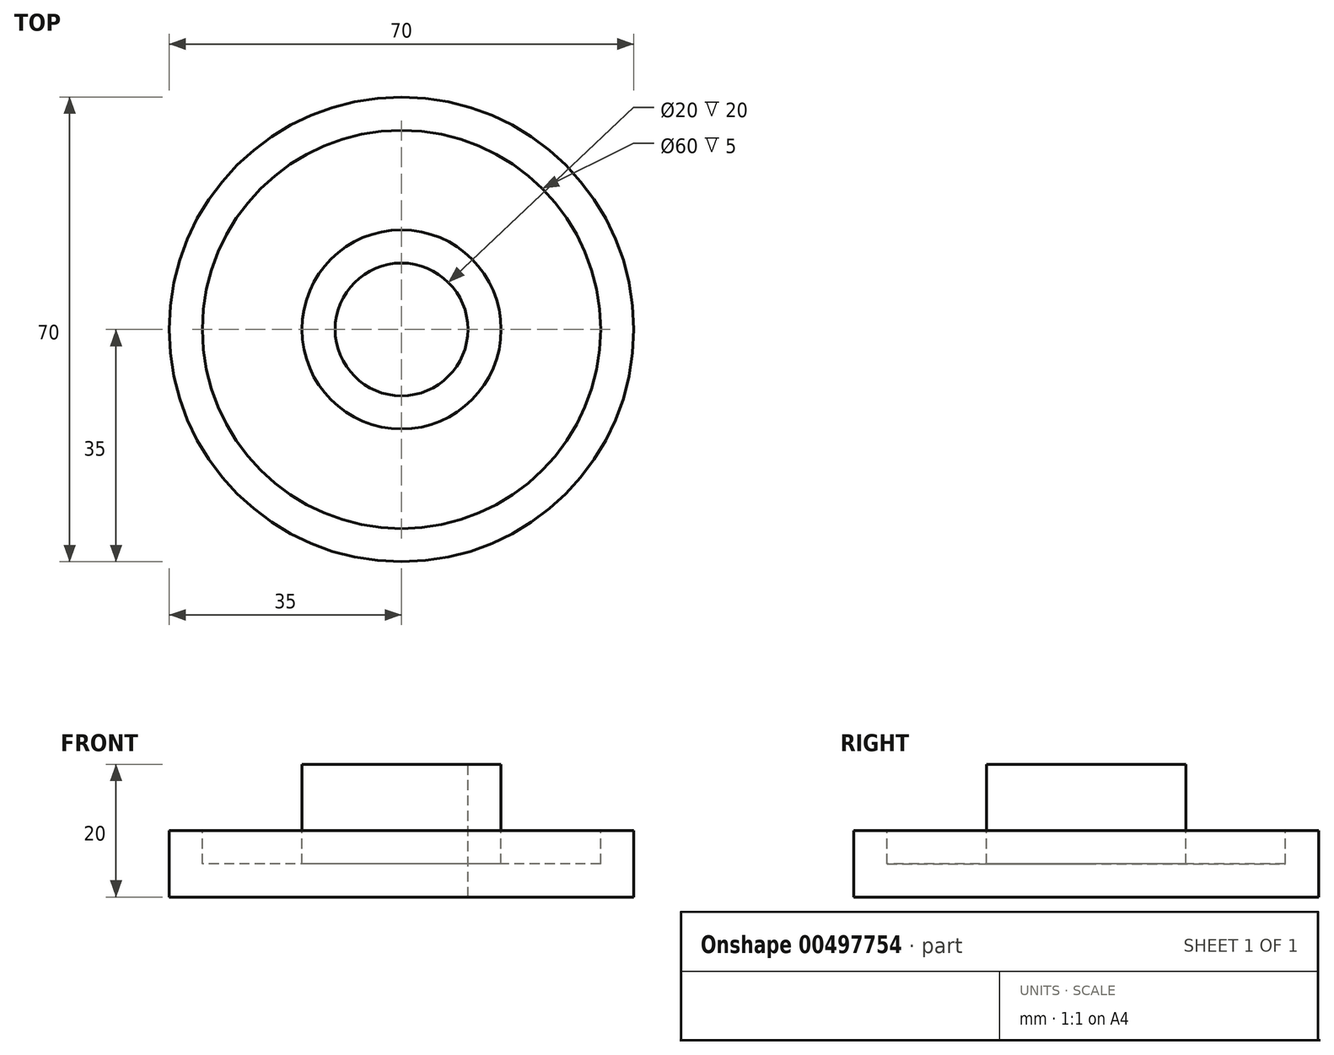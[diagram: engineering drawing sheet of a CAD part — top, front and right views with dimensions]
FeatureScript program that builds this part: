
annotation { "Feature Type Name" : "Feature", "Feature Type Description" : "" }
export const myFeature = defineFeature(function(context is Context, id is Id, definition is map)
    precondition{}
    {
        {
            var Q0;
            Q0=qCreatedBy(makeId("Front.planeOp"),FACE);
            var sketch = newSketch(context, id + "F0", { "sketchPlane" : qUnion([Q0])});
            skLineSegment(sketch, "E0", {"start": v(10, 20) * mm, "end": v(10, 0) * mm});
            skLineSegment(sketch, "E1", {"start": v(10, 0) * mm, "end": v(35, 0) * mm});
            skLineSegment(sketch, "E2", {"start": v(35, 0) * mm, "end": v(35, 10) * mm});
            skLineSegment(sketch, "E3", {"start": v(35, 10) * mm, "end": v(30, 10) * mm});
            skLineSegment(sketch, "E4", {"start": v(30, 10) * mm, "end": v(30, 5) * mm});
            skLineSegment(sketch, "E5", {"start": v(30, 5) * mm, "end": v(15, 5) * mm});
            skLineSegment(sketch, "E6", {"start": v(15, 5) * mm, "end": v(15, 20) * mm});
            skLineSegment(sketch, "E7", {"start": v(15, 20) * mm, "end": v(10, 20) * mm});
            skLineSegment(sketch, "E8", {"start": v(0, 60.65) * mm, "end": v(0, -22.12) * mm, "construction": true});
            skSolve(sketch);
        }
        {
            var Q0;
            Q0=makeQuery(id+"F0.imprint","IMPRINT",FACE,{"disambiguationData":[TD([[makeQuery(id+"F0.imprint","IMPRINT",EDGE,{"derivedFrom":sQuery(id+"F0.wireOp",EDGE,"E0")}),1.0]])]});
            var Q1;
            Q1=sQuery(id+"F0.wireOp",EDGE,"E8");
            revolve(context, id + "F1", {"entities" : qUnion([Q0]), "axis" : qUnion([Q1]), "revolveType" : RevolveType.FULL});
        }
    });
